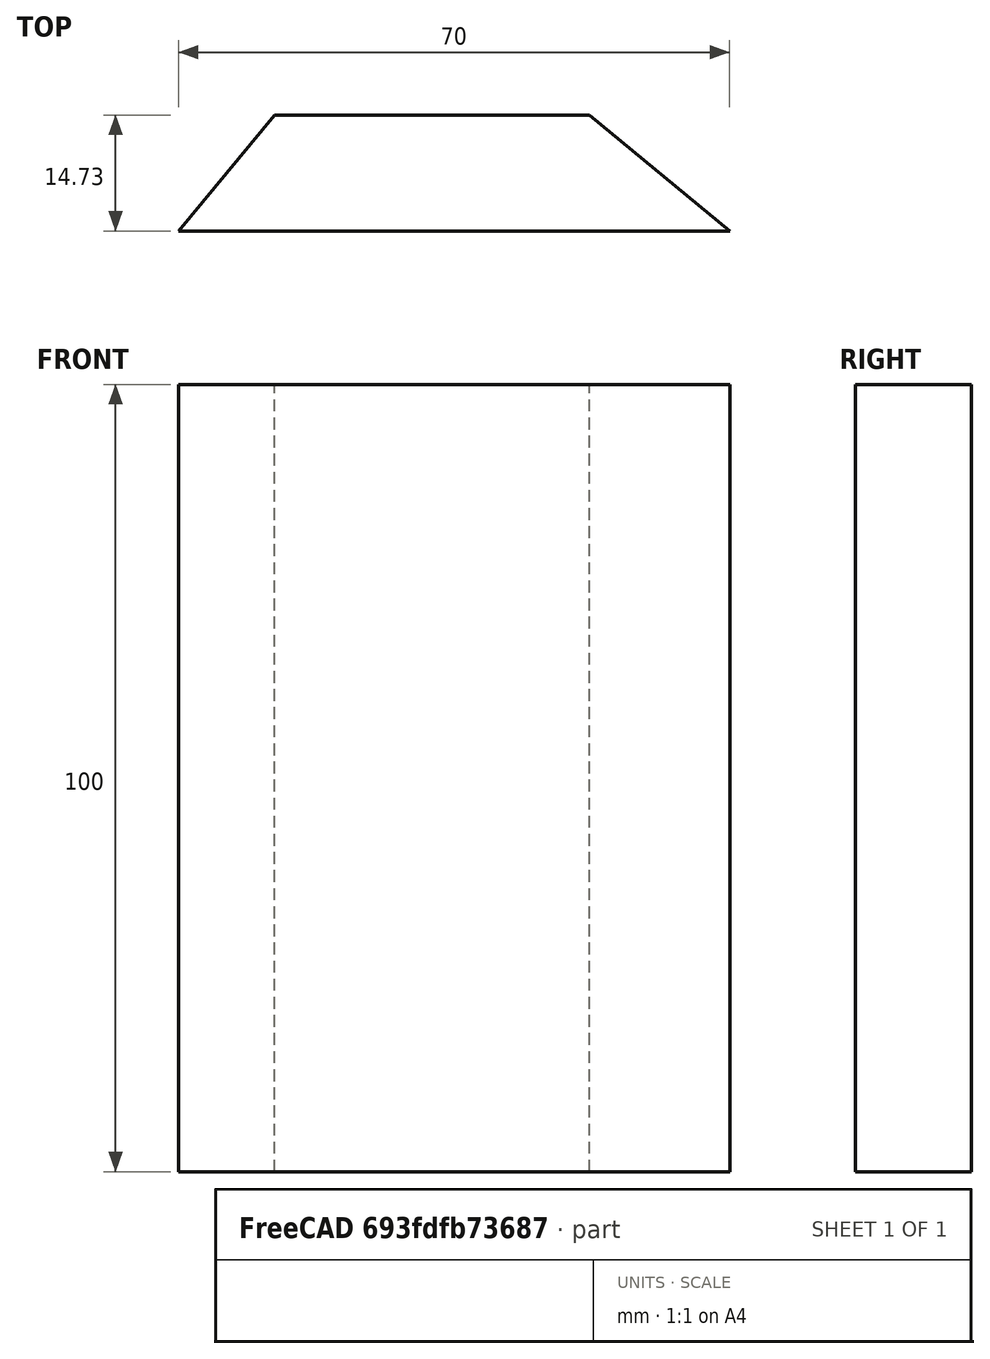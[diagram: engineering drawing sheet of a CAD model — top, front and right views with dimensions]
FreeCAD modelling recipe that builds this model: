
FCSTD DOCUMENT  (FreeCAD 0.18.4R)
Label: lingote_diamante
License: All rights reserved
LicenseURL: http://en.wikipedia.org/wiki/All_rights_reserved
objects: Sketcher::SketchObject×1, PartDesign::Pad×1, PartDesign::Body×1
note: 4 computed .brp shape members not serialized (recipe doc carries the construction recipe); baked Part::Feature solids carry a one-line shape summary decoded from their .brp

FEATURE [Sketcher::SketchObject] Sketch001
  MapMode = 5
  Support = -> [XY_Plane002]
  sketch-geometry (4):
    g0: LineSegment StartX=37.173 StartY=0 StartZ=0 EndX=19.3397 EndY=14.73 EndZ=0
    g1: LineSegment StartX=19.3397 StartY=14.73 StartZ=0 EndX=-20.6603 EndY=14.73 EndZ=0
    g2: LineSegment StartX=-20.6603 StartY=14.73 StartZ=0 EndX=-32.827 EndY=1.8e-15 EndZ=0
    g3: LineSegment StartX=-32.827 StartY=0 StartZ=0 EndX=37.173 EndY=0 EndZ=0
  constraints (10):
    c: Coincident(g0,g1)
    c: Coincident(g1,g2)
    c: Coincident(g2,g3)
    c: Coincident(g3,g0)
    c: Horizontal(g1)
    c: Horizontal(g3)
    c: Perpendicular(g2,g0)
    c: PointOnObject(g0,g-1)
    c: DistanceX(g3,g3) = 70
    c: DistanceX(g1,g1) = 40
FEATURE [PartDesign::Pad] Pad
  Length = 100
  Length2 = 100
  Profile = -> Sketch001
  Refine = true
  Type = 0
FEATURE [PartDesign::Body] Body002
  Group = -> [Sketch001,Pad]
  Origin = -> Origin002
  Tip = -> Pad
